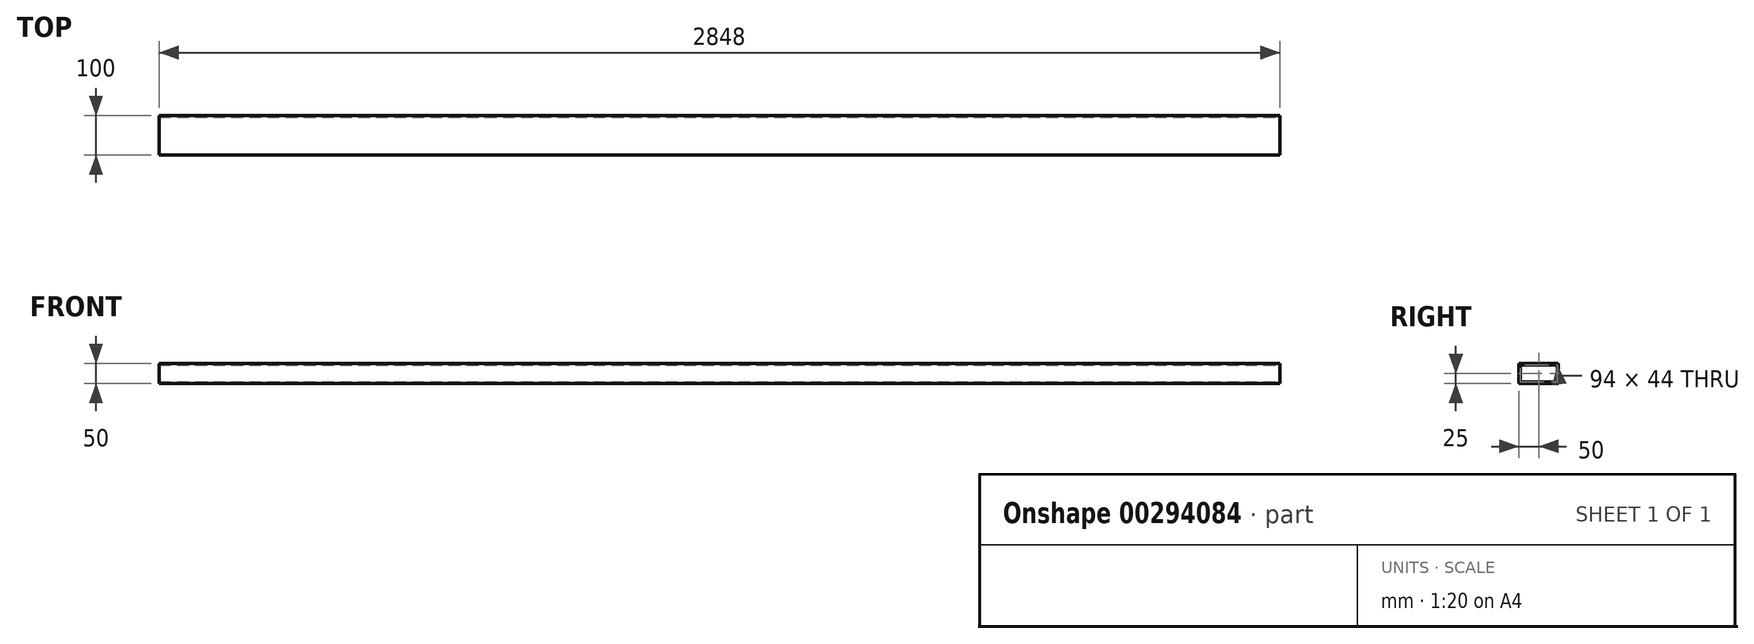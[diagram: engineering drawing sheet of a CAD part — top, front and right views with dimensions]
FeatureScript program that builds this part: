
annotation { "Feature Type Name" : "Feature", "Feature Type Description" : "" }
export const myFeature = defineFeature(function(context is Context, id is Id, definition is map)
    precondition{}
    {
        {
            var Q0;
            Q0=qCreatedBy(makeId("Right.planeOp"),FACE);
            var sketch = newSketch(context, id + "F0", { "sketchPlane" : qUnion([Q0])});
            skLineSegment(sketch, "E0.bottom", {"start": v(50, 25) * mm, "end": v(-50, 25) * mm});
            skLineSegment(sketch, "E0.top", {"start": v(50, -25) * mm, "end": v(-50, -25) * mm});
            skLineSegment(sketch, "E0.left", {"start": v(50, 25) * mm, "end": v(50, -25) * mm});
            skLineSegment(sketch, "E0.right", {"start": v(-50, 25) * mm, "end": v(-50, -25) * mm});
            skPoint(sketch, "E0.middle", {"position": v(0, 0) * mm});
            skLineSegment(sketch, "E1.0", {"start": v(47, -22) * mm, "end": v(-47, -22) * mm});
            skLineSegment(sketch, "E1.1", {"start": v(47, 22) * mm, "end": v(47, -22) * mm});
            skLineSegment(sketch, "E1.2", {"start": v(47, 22) * mm, "end": v(-47, 22) * mm});
            skLineSegment(sketch, "E1.3", {"start": v(-47, 22) * mm, "end": v(-47, -22) * mm});
            skSolve(sketch);
        }
        {
            var Q0;
            Q0 = qSketchRegion(id + "F0", true);
            extrude(context, id + "F1", {"entities" : qUnion([Q0]), "oppositeDirection" : true, "depth" : (3000 - 152) * mm});
        }
    });
